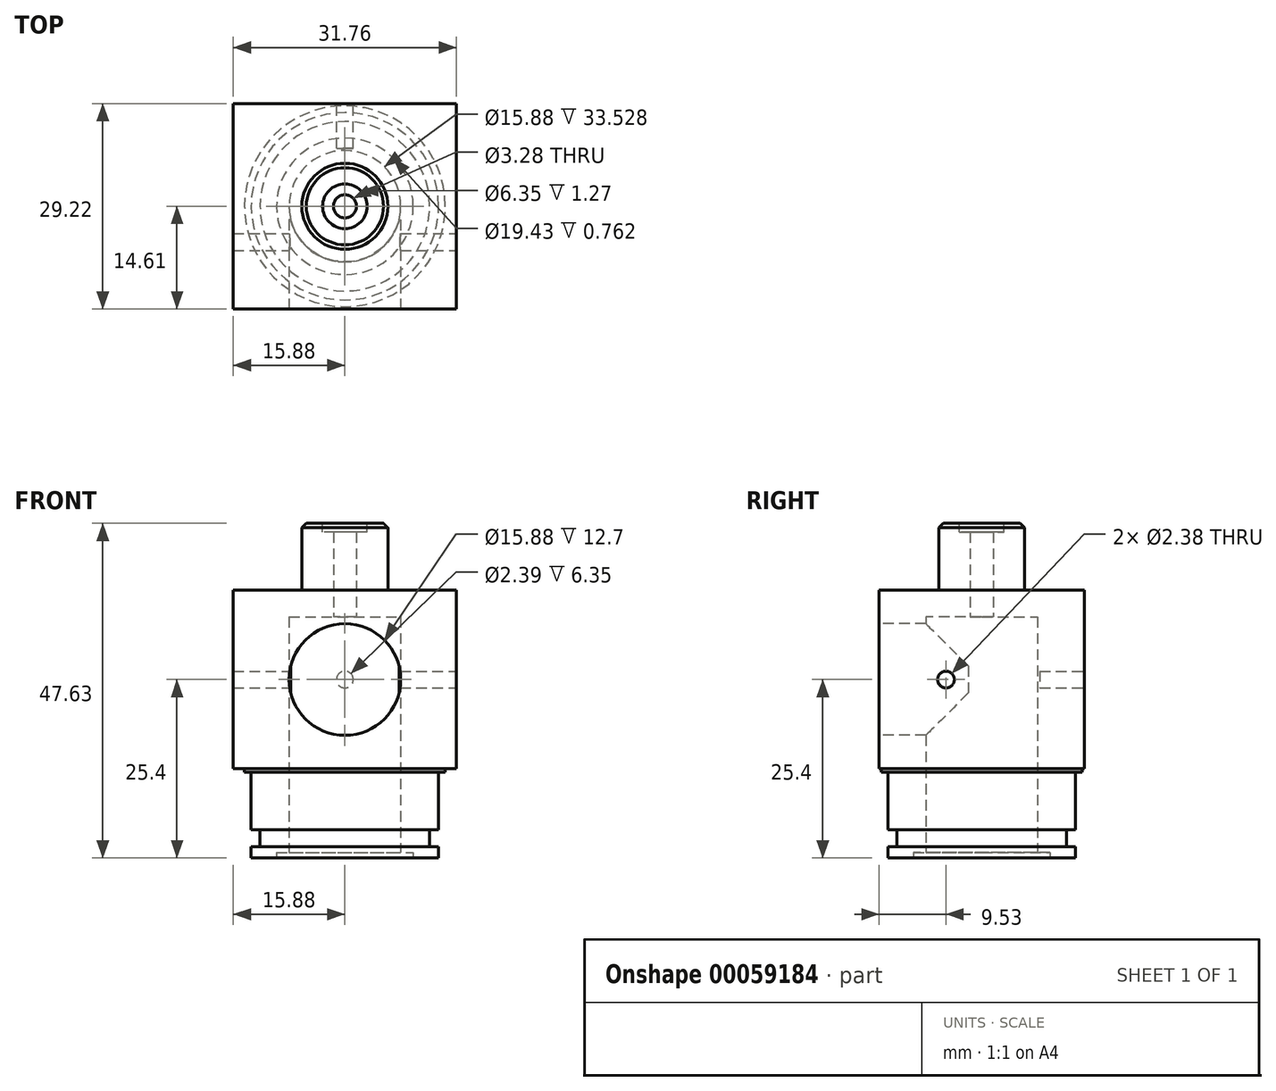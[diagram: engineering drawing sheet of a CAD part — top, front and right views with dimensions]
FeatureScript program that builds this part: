
annotation { "Feature Type Name" : "Feature", "Feature Type Description" : "" }
export const myFeature = defineFeature(function(context is Context, id is Id, definition is map)
    precondition{}
    {
        {
            var Q0;
            Q0=qCreatedBy(makeId("Top.planeOp"),FACE);
            var sketch = newSketch(context, id + "F0", { "sketchPlane" : qUnion([Q0])});
            skLineSegment(sketch, "E0.rect.bottom", {"start": v(15.88, -14.6) * mm, "end": v(-15.88, -14.6) * mm});
            skLineSegment(sketch, "E0.rect.top", {"start": v(15.88, 14.6) * mm, "end": v(-15.88, 14.6) * mm});
            skLineSegment(sketch, "E0.rect.left", {"start": v(15.88, -14.6) * mm, "end": v(15.88, 14.6) * mm});
            skLineSegment(sketch, "E0.rect.right", {"start": v(-15.88, -14.6) * mm, "end": v(-15.88, 14.6) * mm});
            skPoint(sketch, "E0.rect.middle", {"position": v(0, 0) * mm});
            skCircle(sketch, "E1", {"center": v(0, 0) * mm, "radius": 14.29 * mm});
            skCircle(sketch, "E2", {"center": v(0, 0) * mm, "radius": 13.34 * mm});
            skCircle(sketch, "E3", {"center": v(0, 0) * mm, "radius": 1.64 * mm});
            skCircle(sketch, "E4", {"center": v(0, 0) * mm, "radius": 7.94 * mm});
            skSolve(sketch);
        }
        {
            var Q0;
            Q0=makeQuery(id+"F0.imprint","IMPRINT",FACE,{"disambiguationData":[TD([[makeQuery(id+"F0.imprint","IMPRINT",EDGE,{"derivedFrom":sQuery(id+"F0.wireOp",EDGE,"E3")}),-1.0]])]});
            var Q1;
            Q1=makeQuery(id+"F0.imprint","IMPRINT",FACE,{"disambiguationData":[TD([[makeQuery(id+"F0.imprint","IMPRINT",EDGE,{"derivedFrom":sQuery(id+"F0.wireOp",EDGE,"9a5a02ac-67e2-4682-a667-5af901de7d91")}),-1.0]])]});
            var Q2;
            Q2=makeQuery(id+"F0.imprint","IMPRINT",FACE,{"disambiguationData":[TD([[makeQuery(id+"F0.imprint","IMPRINT",EDGE,{"derivedFrom":sQuery(id+"F0.wireOp",EDGE,"E2")}),1.0]])]});
            var Q3;
            Q3=makeQuery(id+"F0.imprint","IMPRINT",FACE,{"disambiguationData":[TD([[makeQuery(id+"F0.imprint","IMPRINT",EDGE,{"derivedFrom":sQuery(id+"F0.wireOp",EDGE,"E1")}),1.0]])]});
            var Q4;
            Q4=makeQuery(id+"F0.imprint","IMPRINT",FACE,{"disambiguationData":[TD([[makeQuery(id+"F0.imprint","IMPRINT",EDGE,{"derivedFrom":sQuery(id+"F0.wireOp",EDGE,"E0.rect.bottom")}),-1.0]])]});
            var Q5;
            Q5=makeQuery(id+"F0.imprint","IMPRINT",FACE,{"disambiguationData":[TD([[makeQuery(id+"F0.imprint","IMPRINT",EDGE,{"derivedFrom":sQuery(id+"F0.wireOp",EDGE,"9a5a02ac-67e2-4682-a667-5af901de7d91")}),1.0]])]});
            extrude(context, id + "F1", {"entities" : qUnion([Q0, Q1, Q2, Q3, Q4, Q5]), "depth" : 25.4 * mm});
        }
        {
            var Q0;
            Q0=makeQuery(id+"F1.opExtrude","CAP_FACE",FACE,{"disambiguationData":[OSD([sQuery(id+"F0.wireOp",EDGE,"E0.rect.bottom"),sQuery(id+"F0.wireOp",EDGE,"E0.rect.top"),sQuery(id+"F0.wireOp",EDGE,"E0.rect.left"),sQuery(id+"F0.wireOp",EDGE,"E0.rect.right"),sQuery(id+"F0.wireOp",EDGE,"E3")])],"isStart":false});
            var sketch = newSketch(context, id + "F2", { "sketchPlane" : qUnion([Q0])});
            skCircle(sketch, "E5", {"center": v(0, 0) * mm, "radius": 6.12 * mm});
            skSolve(sketch);
        }
        {
            var Q0;
            Q0=makeQuery(id+"F2.imprint","IMPRINT",FACE,{"disambiguationData":[TD([[makeQuery(id+"F2.imprint","IMPRINT",EDGE,{"derivedFrom":sQuery(id+"F2.wireOp",EDGE,"E5")}),1.0]])]});
            extrude(context, id + "F3", {"entities" : qUnion([Q0]), "operationType" : NewBodyOperationType.ADD, "depth" : 9.52 * mm});
        }
        {
            var Q0;
            Q0=makeQuery(id+"F3.opExtrude","CAP_FACE",FACE,{"disambiguationData":[OSD([sQuery(id+"F0.wireOp",EDGE,"E3"),sQuery(id+"F2.wireOp",EDGE,"E5")])],"isStart":false});
            var sketch = newSketch(context, id + "F4", { "sketchPlane" : qUnion([Q0])});
            skCircle(sketch, "E6", {"center": v(0, 0) * mm, "radius": 3.18 * mm});
            skSolve(sketch);
        }
        {
            var Q0;
            Q0=makeQuery(id+"F4.imprint","IMPRINT",FACE,{"disambiguationData":[TD([[makeQuery(id+"F4.imprint","IMPRINT",EDGE,{"derivedFrom":sQuery(id+"F4.wireOp",EDGE,"E6")}),1.0]])]});
            extrude(context, id + "F5", {"entities" : qUnion([Q0]), "operationType" : NewBodyOperationType.REMOVE, "oppositeDirection" : true, "depth" : 1.27 * mm});
        }
        {
            var Q0;
            Q0=makeQuery(id+"F0.imprint","IMPRINT",FACE,{"disambiguationData":[TD([[makeQuery(id+"F0.imprint","IMPRINT",EDGE,{"derivedFrom":sQuery(id+"F0.wireOp",EDGE,"E3")}),-1.0]])]});
            var sketch = newSketch(context, id + "F6", { "sketchPlane" : qUnion([Q0])});
            skCircle(sketch, "E7", {"center": v(0, 0) * mm, "radius": 7.94 * mm});
            skSolve(sketch);
        }
        {
            var Q0;
            Q0=makeQuery(id+"F0.imprint","IMPRINT",FACE,{"disambiguationData":[TD([[makeQuery(id+"F0.imprint","IMPRINT",EDGE,{"derivedFrom":sQuery(id+"F0.wireOp",EDGE,"E3")}),-1.0]])]});
            extrude(context, id + "F7", {"entities" : qUnion([Q0]), "operationType" : NewBodyOperationType.REMOVE, "depth" : 21.59 * mm});
        }
        {
            var Q0;
            Q0=makeQuery(id+"F3.opExtrude","CAP_EDGE",EDGE,{"disambiguationData":[OSD([sQuery(id+"F2.wireOp",EDGE,"E5")])],"isStart":false});
            chamfer(context, id + "F8", {"entities" : qUnion([Q0]), "width" : 0.64 * mm, "tangentPropagation" : true});
        }
        {
            var Q0;
            Q0=makeQuery(id+"F1.opExtrude","SWEPT_FACE",FACE,{"disambiguationData":[OSD([sQuery(id+"F0.wireOp",EDGE,"E0.rect.bottom")])]});
            var sketch = newSketch(context, id + "F9", { "sketchPlane" : qUnion([Q0])});
            skCircle(sketch, "E8", {"center": v(0, 12.7) * mm, "radius": 7.94 * mm});
            skSolve(sketch);
        }
        {
            var Q0;
            Q0=makeQuery(id+"F9.imprint","IMPRINT",FACE,{"disambiguationData":[TD([[makeQuery(id+"F9.imprint","IMPRINT",EDGE,{"derivedFrom":sQuery(id+"F9.wireOp",EDGE,"E8")}),1.0]])]});
            extrude(context, id + "F10", {"entities" : qUnion([Q0]), "operationType" : NewBodyOperationType.REMOVE, "oppositeDirection" : true, "depth" : 12.7 * mm});
        }
        {
            var Q0;
            Q0=makeQuery(id+"F1.opExtrude","SWEPT_FACE",FACE,{"disambiguationData":[OSD([sQuery(id+"F0.wireOp",EDGE,"E0.rect.top")])]});
            var sketch = newSketch(context, id + "F11", { "sketchPlane" : qUnion([Q0])});
            skCircle(sketch, "E9", {"center": v(0, 12.7) * mm, "radius": 1.2 * mm});
            skSolve(sketch);
        }
        {
            var Q0;
            Q0=makeQuery(id+"F11.imprint","IMPRINT",FACE,{"disambiguationData":[TD([[makeQuery(id+"F11.imprint","IMPRINT",EDGE,{"derivedFrom":sQuery(id+"F11.wireOp",EDGE,"E9")}),1.0]])]});
            extrude(context, id + "F12", {"entities" : qUnion([Q0]), "operationType" : NewBodyOperationType.REMOVE, "oppositeDirection" : true, "depth" : 6.35 * mm});
        }
        {
            var Q0;
            Q0=makeQuery(id+"F1.opExtrude","SWEPT_FACE",FACE,{"disambiguationData":[OSD([sQuery(id+"F0.wireOp",EDGE,"E0.rect.left")])]});
            var sketch = newSketch(context, id + "F13", { "sketchPlane" : qUnion([Q0])});
            skCircle(sketch, "E10", {"center": v(-5.08, 12.7) * mm, "radius": 1.2 * mm});
            skSolve(sketch);
        }
        {
            var Q0;
            Q0=makeQuery(id+"F13.imprint","IMPRINT",FACE,{"disambiguationData":[TD([[makeQuery(id+"F13.imprint","IMPRINT",EDGE,{"derivedFrom":sQuery(id+"F13.wireOp",EDGE,"E10")}),1.0]])]});
            extrude(context, id + "F14", {"entities" : qUnion([Q0]), "operationType" : NewBodyOperationType.REMOVE, "endBound" : BoundingType.THROUGH_ALL, "oppositeDirection" : true, "depth" : 25.4 * mm});
        }
        {
            var Q0;
            Q0=qCreatedBy(makeId("Front.planeOp"),FACE);
            var sketch = newSketch(context, id + "F15", { "sketchPlane" : qUnion([Q0])});
            skLineSegment(sketch, "E11", {"start": v(0, -12.7) * mm, "end": v(0, -12.75) * mm});
            skLineSegment(sketch, "E12", {"start": v(0, -12.7) * mm, "end": v(13.34, -12.7) * mm});
            skLineSegment(sketch, "E13", {"start": v(13.34, -12.7) * mm, "end": v(13.34, -11.11) * mm});
            skLineSegment(sketch, "E14", {"start": v(13.34, -11.11) * mm, "end": v(12.07, -11.11) * mm});
            skLineSegment(sketch, "E15", {"start": v(12.07, -11.11) * mm, "end": v(12.07, -8.7) * mm});
            skLineSegment(sketch, "E16", {"start": v(12.07, -8.7) * mm, "end": v(13.34, -8.7) * mm});
            skLineSegment(sketch, "E17", {"start": v(13.34, -8.7) * mm, "end": v(13.34, -0.5) * mm});
            skLineSegment(sketch, "E18", {"start": v(13.34, -0.5) * mm, "end": v(14.29, -0.5) * mm});
            skLineSegment(sketch, "E19", {"start": v(14.29, -0.5) * mm, "end": v(14.29, 0) * mm});
            skLineSegment(sketch, "E20", {"start": v(14.29, 0) * mm, "end": v(0, 0) * mm});
            skLineSegment(sketch, "E21", {"start": v(0, 0) * mm, "end": v(0, -12.7) * mm});
            skSolve(sketch);
        }
        {
            var Q0;
            Q0=makeQuery(id+"F15.imprint","IMPRINT",FACE,{"disambiguationData":[TD([[makeQuery(id+"F15.imprint","IMPRINT",EDGE,{"derivedFrom":sQuery(id+"F15.wireOp",EDGE,"E12")}),1.0]])]});
            var Q1;
            Q1=sQuery(id+"F15.wireOp",EDGE,"E21");
            revolve(context, id + "F16", {"operationType" : NewBodyOperationType.ADD, "entities" : qUnion([Q0]), "axis" : qUnion([Q1]), "revolveType" : RevolveType.FULL});
        }
        {
            var Q0;
            Q0=makeQuery(id+"F16.opRevolve","SWEPT_FACE",FACE,{"disambiguationData":[OSD([sQuery(id+"F15.wireOp",EDGE,"E12")])]});
            var sketch = newSketch(context, id + "F17", { "sketchPlane" : qUnion([Q0])});
            skCircle(sketch, "E22", {"center": v(0, 0) * mm, "radius": 7.94 * mm});
            skSolve(sketch);
        }
        {
            var Q0;
            Q0=makeQuery(id+"F17.imprint","IMPRINT",FACE,{"disambiguationData":[TD([[makeQuery(id+"F17.imprint","IMPRINT",EDGE,{"derivedFrom":sQuery(id+"F17.wireOp",EDGE,"E22")}),1.0]])]});
            extrude(context, id + "F18", {"entities" : qUnion([Q0]), "operationType" : NewBodyOperationType.REMOVE, "oppositeDirection" : true, "depth" : 12.7 * mm});
        }
        {
            var Q0;
            Q0=makeQuery(id+"F16.opRevolve","SWEPT_FACE",FACE,{"disambiguationData":[OSD([sQuery(id+"F15.wireOp",EDGE,"E12")])]});
            var sketch = newSketch(context, id + "F19", { "sketchPlane" : qUnion([Q0])});
            skCircle(sketch, "E23", {"center": v(0, 0) * mm, "radius": 9.72 * mm});
            skSolve(sketch);
        }
        {
            var Q0;
            Q0 = qSketchRegion(id + "F19", true);
            extrude(context, id + "F20", {"entities" : qUnion([Q0]), "operationType" : NewBodyOperationType.REMOVE, "oppositeDirection" : true, "depth" : 0.76 * mm});
        }
    });
